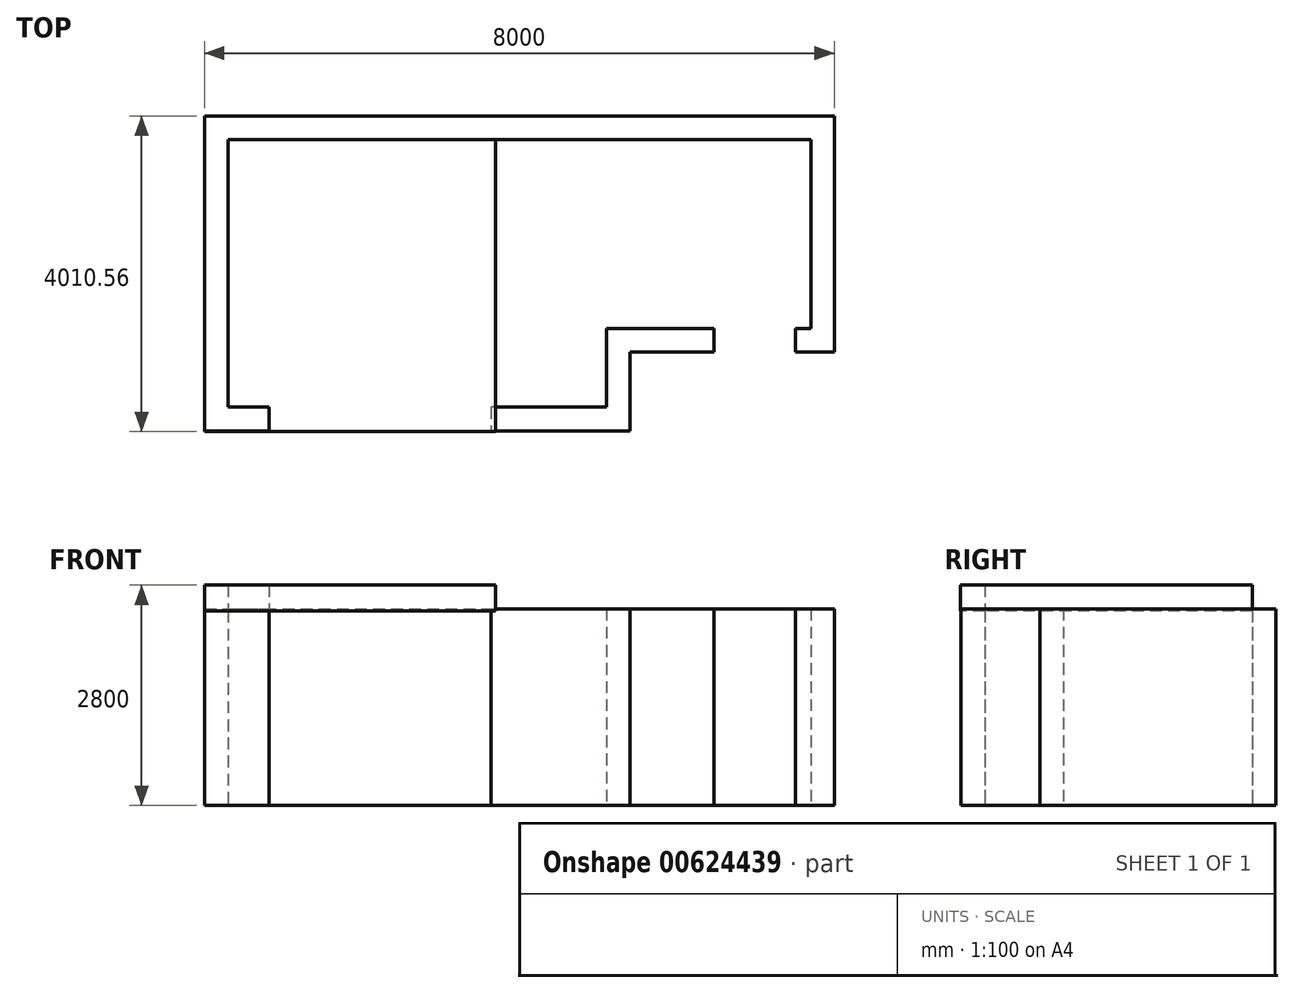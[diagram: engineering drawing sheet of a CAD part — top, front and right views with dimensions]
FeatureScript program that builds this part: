
annotation { "Feature Type Name" : "Feature", "Feature Type Description" : "" }
export const myFeature = defineFeature(function(context is Context, id is Id, definition is map)
    precondition{}
    {
        {
            var Q0;
            Q0=qCreatedBy(makeId("Top.planeOp"),FACE);
            var sketch = newSketch(context, id + "F0", { "sketchPlane" : qUnion([Q0])});
            skLineSegment(sketch, "E0", {"start": v(-4028.19, 1693.53) * mm, "end": v(-4028.19, -2306.47) * mm});
            skLineSegment(sketch, "E1", {"start": v(-4028.19, -2306.47) * mm, "end": v(-3206.02, -2306.47) * mm});
            skLineSegment(sketch, "E2", {"start": v(-4028.19, 1693.53) * mm, "end": v(3971.81, 1693.53) * mm});
            skLineSegment(sketch, "E3", {"start": v(3971.81, 1693.53) * mm, "end": v(3971.81, -1306.47) * mm});
            skLineSegment(sketch, "E4", {"start": v(3971.81, -1306.47) * mm, "end": v(3475.89, -1306.47) * mm});
            skLineSegment(sketch, "E5", {"start": v(2441.32, -1306.47) * mm, "end": v(1377.9, -1306.47) * mm});
            skLineSegment(sketch, "E6", {"start": v(1377.9, -1306.47) * mm, "end": v(1377.9, -2306.47) * mm});
            skLineSegment(sketch, "E7", {"start": v(1377.9, -2306.47) * mm, "end": v(-391.82, -2306.47) * mm});
            skLineSegment(sketch, "E8.0", {"start": v(1077.9, -2006.47) * mm, "end": v(-391.82, -2006.47) * mm});
            skLineSegment(sketch, "E8.1", {"start": v(1077.9, -1006.47) * mm, "end": v(1077.9, -2006.47) * mm});
            skLineSegment(sketch, "E8.2", {"start": v(2441.32, -1006.47) * mm, "end": v(1077.9, -1006.47) * mm});
            skLineSegment(sketch, "E9.0", {"start": v(3671.81, -1006.47) * mm, "end": v(3475.89, -1006.47) * mm});
            skLineSegment(sketch, "E9.1", {"start": v(-3728.19, -2006.47) * mm, "end": v(-3206.02, -2006.47) * mm});
            skLineSegment(sketch, "E9.2", {"start": v(-3728.19, 1393.53) * mm, "end": v(-3728.19, -2006.47) * mm});
            skLineSegment(sketch, "E9.3", {"start": v(-3728.19, 1393.53) * mm, "end": v(3671.81, 1393.53) * mm});
            skLineSegment(sketch, "E9.4", {"start": v(3671.81, 1393.53) * mm, "end": v(3671.81, -1006.47) * mm});
            skLineSegment(sketch, "E10", {"start": v(3475.89, -1006.47) * mm, "end": v(3475.89, -1306.47) * mm});
            skLineSegment(sketch, "E11", {"start": v(2441.32, -1006.47) * mm, "end": v(2441.32, -1306.47) * mm});
            skLineSegment(sketch, "E12", {"start": v(-391.82, -2006.47) * mm, "end": v(-391.82, -2306.47) * mm});
            skLineSegment(sketch, "E13", {"start": v(-3206.02, -2006.47) * mm, "end": v(-3206.02, -2306.47) * mm});
            skSolve(sketch);
        }
        {
            var Q0;
            Q0=makeQuery(id+"F0.imprint","IMPRINT",FACE,{"disambiguationData":[TD([[makeQuery(id+"F0.imprint","IMPRINT",EDGE,{"derivedFrom":sQuery(id+"F0.wireOp",EDGE,"E0")}),1.0]])]});
            var Q1;
            Q1=makeQuery(id+"F0.imprint","IMPRINT",FACE,{"disambiguationData":[TD([[makeQuery(id+"F0.imprint","IMPRINT",EDGE,{"derivedFrom":sQuery(id+"F0.wireOp",EDGE,"E5")}),-1.0]])]});
            extrude(context, id + "F1", {"entities" : qUnion([Q0, Q1]), "depth" : 2500 * mm, "offsetDistance" : 25 * mm});
        }
        {
            var Q0;
            Q0=makeQuery(id+"F1.opExtrude","CAP_FACE",FACE,{"disambiguationData":[OSD([sQuery(id+"F0.wireOp",EDGE,"E0"),sQuery(id+"F0.wireOp",EDGE,"E1"),sQuery(id+"F0.wireOp",EDGE,"E2"),sQuery(id+"F0.wireOp",EDGE,"E3"),sQuery(id+"F0.wireOp",EDGE,"E4"),sQuery(id+"F0.wireOp",EDGE,"E9.0"),sQuery(id+"F0.wireOp",EDGE,"E9.1"),sQuery(id+"F0.wireOp",EDGE,"E9.2"),sQuery(id+"F0.wireOp",EDGE,"E9.3"),sQuery(id+"F0.wireOp",EDGE,"E9.4"),sQuery(id+"F0.wireOp",EDGE,"E10"),sQuery(id+"F0.wireOp",EDGE,"E13")])],"isStart":false});
            var sketch = newSketch(context, id + "F2", { "sketchPlane" : qUnion([Q0])});
            skLineSegment(sketch, "E14.bottom", {"start": v(-4028.19, 1693.53) * mm, "end": v(-332.28, 1693.53) * mm});
            skLineSegment(sketch, "E14.top", {"start": v(-4028.19, -2317.03) * mm, "end": v(-332.28, -2317.03) * mm});
            skLineSegment(sketch, "E14.left", {"start": v(-4028.19, 1693.53) * mm, "end": v(-4028.19, -2317.03) * mm});
            skLineSegment(sketch, "E14.right", {"start": v(-332.28, 1693.53) * mm, "end": v(-332.28, -2317.03) * mm});
            skSolve(sketch);
        }
        {
            var Q0;
            {var subQ1=sQuery(id+"F2.wireOp",EDGE,"E14.top");Q0=makeQuery(id+"F2.imprint","IMPRINT",FACE,{"disambiguationData":[TD([[makeQuery(id+"F2.imprint","IMPRINT",EDGE,{"derivedFrom":subQ1}),1.0]])]});}
            extrude(context, id + "F3", {"entities" : qUnion([Q0]), "operationType" : NewBodyOperationType.ADD, "depth" : 300 * mm, "offsetDistance" : 25 * mm, "hasSecondDirection" : true, "secondDirectionOppositeDirection" : true, "secondDirectionDepth" : 25 * mm});
        }
    });
